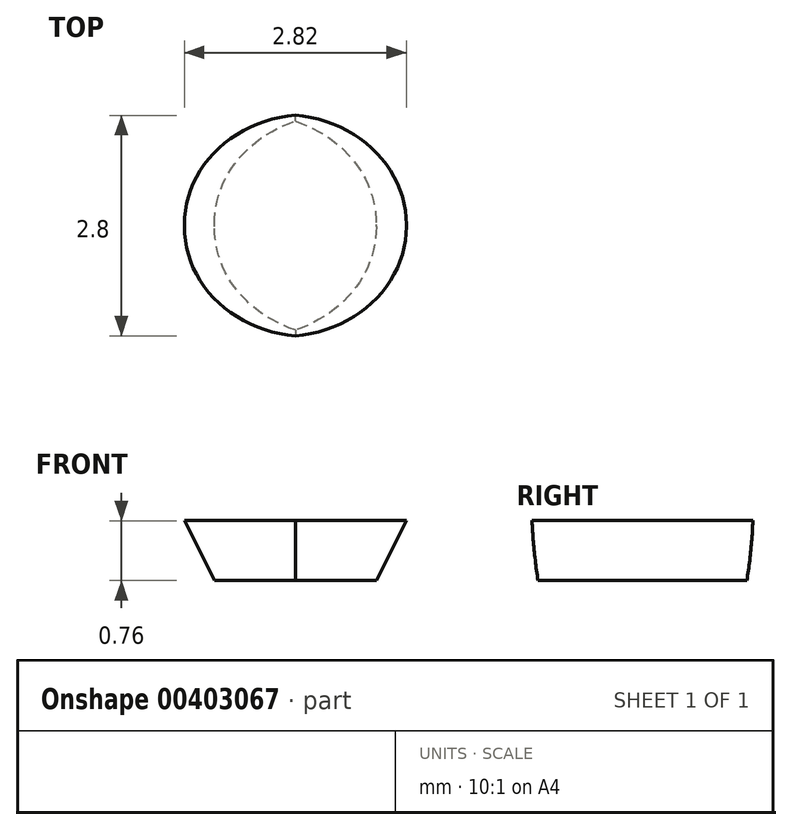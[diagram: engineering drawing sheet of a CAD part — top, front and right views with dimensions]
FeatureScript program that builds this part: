
annotation { "Feature Type Name" : "Feature", "Feature Type Description" : "" }
export const myFeature = defineFeature(function(context is Context, id is Id, definition is map)
    precondition{}
    {
        {
            var Q0;
            Q0=qCreatedBy(makeId("Front.planeOp"),FACE);
            var sketch = newSketch(context, id + "F0", { "sketchPlane" : qUnion([Q0])});
            skLineSegment(sketch, "E0.top", {"start": v(1.03, -0.38) * mm, "end": v(-1.03, -0.38) * mm});
            skLineSegment(sketch, "E1", {"start": v(-1.4, 0.38) * mm, "end": v(1.4, 0.38) * mm});
            skLineSegment(sketch, "E2", {"start": v(-1.4, 0.38) * mm, "end": v(-1.03, -0.38) * mm});
            skLineSegment(sketch, "E3", {"start": v(1.03, -0.38) * mm, "end": v(1.4, 0.38) * mm});
            skSolve(sketch);
        }
        {
            var Q0;
            Q0=makeQuery(id+"F0.imprint","IMPRINT",FACE,{"disambiguationData":[TD([[makeQuery(id+"F0.imprint","IMPRINT",EDGE,{"derivedFrom":sQuery(id+"F0.wireOp",EDGE,"E0.top")}),-1.0]])]});
            extrude(context, id + "F1", {"entities" : qUnion([Q0]), "endBound" : BoundingType.SYMMETRIC, "depth" : 2.82 * mm});
        }
        {
            var Q0;
            Q0=makeQuery(id+"F1.opExtrude","CAP_EDGE",EDGE,{"disambiguationData":[OSD([sQuery(id+"F0.wireOp",EDGE,"E2")])],"isStart":true});
            var Q1;
            Q1=makeQuery(id+"F1.opExtrude","CAP_EDGE",EDGE,{"disambiguationData":[OSD([sQuery(id+"F0.wireOp",EDGE,"E2")])],"isStart":false});
            var Q2;
            Q2=makeQuery(id+"F1.opExtrude","CAP_EDGE",EDGE,{"disambiguationData":[OSD([sQuery(id+"F0.wireOp",EDGE,"E3")])],"isStart":false});
            var Q3;
            Q3=makeQuery(id+"F1.opExtrude","CAP_EDGE",EDGE,{"disambiguationData":[OSD([sQuery(id+"F0.wireOp",EDGE,"E3")])],"isStart":true});
            fillet(context, id + "F2", {"entities" : qUnion([Q0, Q1, Q2, Q3]), "radius" : 1.4 * mm, "allowEdgeOverflow" : false});
        }
    });
